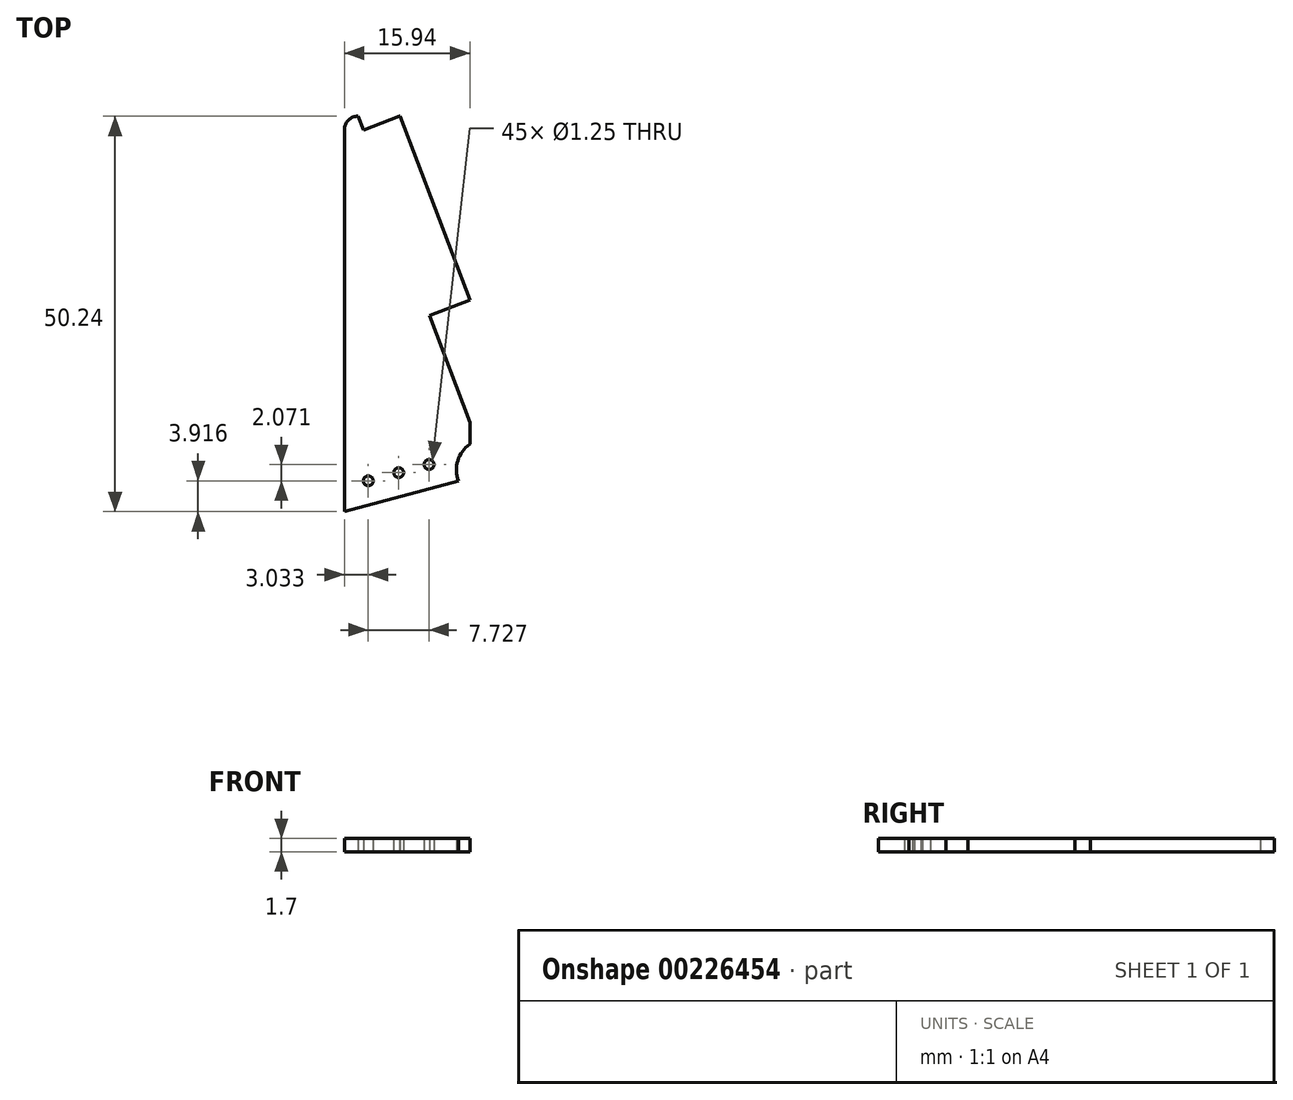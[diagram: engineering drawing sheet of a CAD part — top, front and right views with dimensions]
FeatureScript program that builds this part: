
annotation { "Feature Type Name" : "Feature", "Feature Type Description" : "" }
export const myFeature = defineFeature(function(context is Context, id is Id, definition is map)
    precondition{}
    {
        {
            var Q0;
            Q0=qCreatedBy(makeId("Top.planeOp"),FACE);
            var sketch = newSketch(context, id + "F0", { "sketchPlane" : qUnion([Q0])});
            skLineSegment(sketch, "E0.bottom", {"start": v(-13.86, 11.1) * mm, "end": v(0.33, 11.1) * mm});
            skLineSegment(sketch, "E0.top", {"start": v(-15.6, -39.14) * mm, "end": v(0.33, -39.14) * mm});
            skLineSegment(sketch, "E0.left", {"start": v(-15.6, 9.35) * mm, "end": v(-15.6, -39.14) * mm});
            skLineSegment(sketch, "E0.right", {"start": v(0.33, 11.1) * mm, "end": v(0.33, -39.14) * mm});
            skPoint(sketch, "E1.visualSharp", {"position": v(-15.6, 11.1) * mm});
            skArc(sketch, "E1.filletArc", {"start": v(-13.86, 11.1) * mm, "mid": v(-15.1, 10.6) * mm, "end": v(-15.6, 9.35) * mm});
            skLineSegment(sketch, "E2", {"start": v(-13.86, 11.1) * mm, "end": v(-13.2, 9.35) * mm});
            skLineSegment(sketch, "E3", {"start": v(-13.2, 9.35) * mm, "end": v(-8.52, 11.12) * mm});
            skLineSegment(sketch, "E4", {"start": v(-8.52, 11.12) * mm, "end": v(-5.33, 2.7) * mm});
            skLineSegment(sketch, "E5", {"start": v(-5.33, 2.7) * mm, "end": v(-5.33, 2.7) * mm});
            skLineSegment(sketch, "E6", {"start": v(-5.33, 2.7) * mm, "end": v(-2.85, -3.84) * mm});
            skLineSegment(sketch, "E7", {"start": v(-2.85, -3.84) * mm, "end": v(-2.85, -3.84) * mm});
            skLineSegment(sketch, "E8", {"start": v(-2.85, -3.84) * mm, "end": v(0.33, -12.26) * mm});
            skLineSegment(sketch, "E9", {"start": v(0.33, -12.26) * mm, "end": v(-4.81, -14.2) * mm});
            skLineSegment(sketch, "E10", {"start": v(-4.81, -14.2) * mm, "end": v(1.2, -30.1) * mm});
            skLineSegment(sketch, "E11", {"start": v(1.2, -30.1) * mm, "end": v(1.2, -30.1) * mm});
            skLineSegment(sketch, "E12", {"start": v(-1.12, -35.26) * mm, "end": v(-1.12, -35.26) * mm});
            skPoint(sketch, "E13.visualSharp", {"position": v(-2.53, -31.52) * mm});
            skArc(sketch, "E13.filletArc", {"start": v(1.2, -30.1) * mm, "mid": v(-1.02, -32.2) * mm, "end": v(-1.12, -35.26) * mm});
            skLineSegment(sketch, "E14", {"start": v(-1.12, -35.26) * mm, "end": v(-15.6, -39.14) * mm});
            skCircle(sketch, "E15", {"center": v(-12.58, -35.22) * mm, "radius": 0.62 * mm});
            skCircle(sketch, "E16", {"center": v(-8.71, -34.19) * mm, "radius": 0.62 * mm});
            skCircle(sketch, "E17", {"center": v(-4.85, -33.15) * mm, "radius": 0.62 * mm});
            skLineSegment(sketch, "E18", {"start": v(-15.6, -36.04) * mm, "end": v(-0.99, -32.12) * mm, "construction": true});
            skLineSegment(sketch, "E19", {"start": v(-8.71, -34.19) * mm, "end": v(-4.85, -33.15) * mm});
            skLineSegment(sketch, "E20", {"start": v(-8.71, -34.19) * mm, "end": v(-12.58, -35.22) * mm});
            skLineSegment(sketch, "E21", {"start": v(-12.58, -35.22) * mm, "end": v(-15.6, -36.04) * mm});
            skSolve(sketch);
        }
        {
            var Q0;
            {var subQ17=sQuery(id+"F0.wireOp",EDGE,"E1.filletArc");Q0=makeQuery(id+"F0.imprint","IMPRINT",FACE,{"disambiguationData":[TD([[makeQuery(id+"F0.imprint","IMPRINT",EDGE,{"derivedFrom":subQ17}),1.0]])]});}
            var Q1;
            {var subQ5=sQuery(id+"F0.wireOp",EDGE,"E14");Q1=makeQuery(id+"F0.imprint","IMPRINT",FACE,{"disambiguationData":[TD([[makeQuery(id+"F0.imprint","IMPRINT",EDGE,{"derivedFrom":subQ5}),-1.0]])]});}
            extrude(context, id + "F1", {"entities" : qUnion([Q0, Q1]), "depth" : 1.7 * mm});
        }
    });
